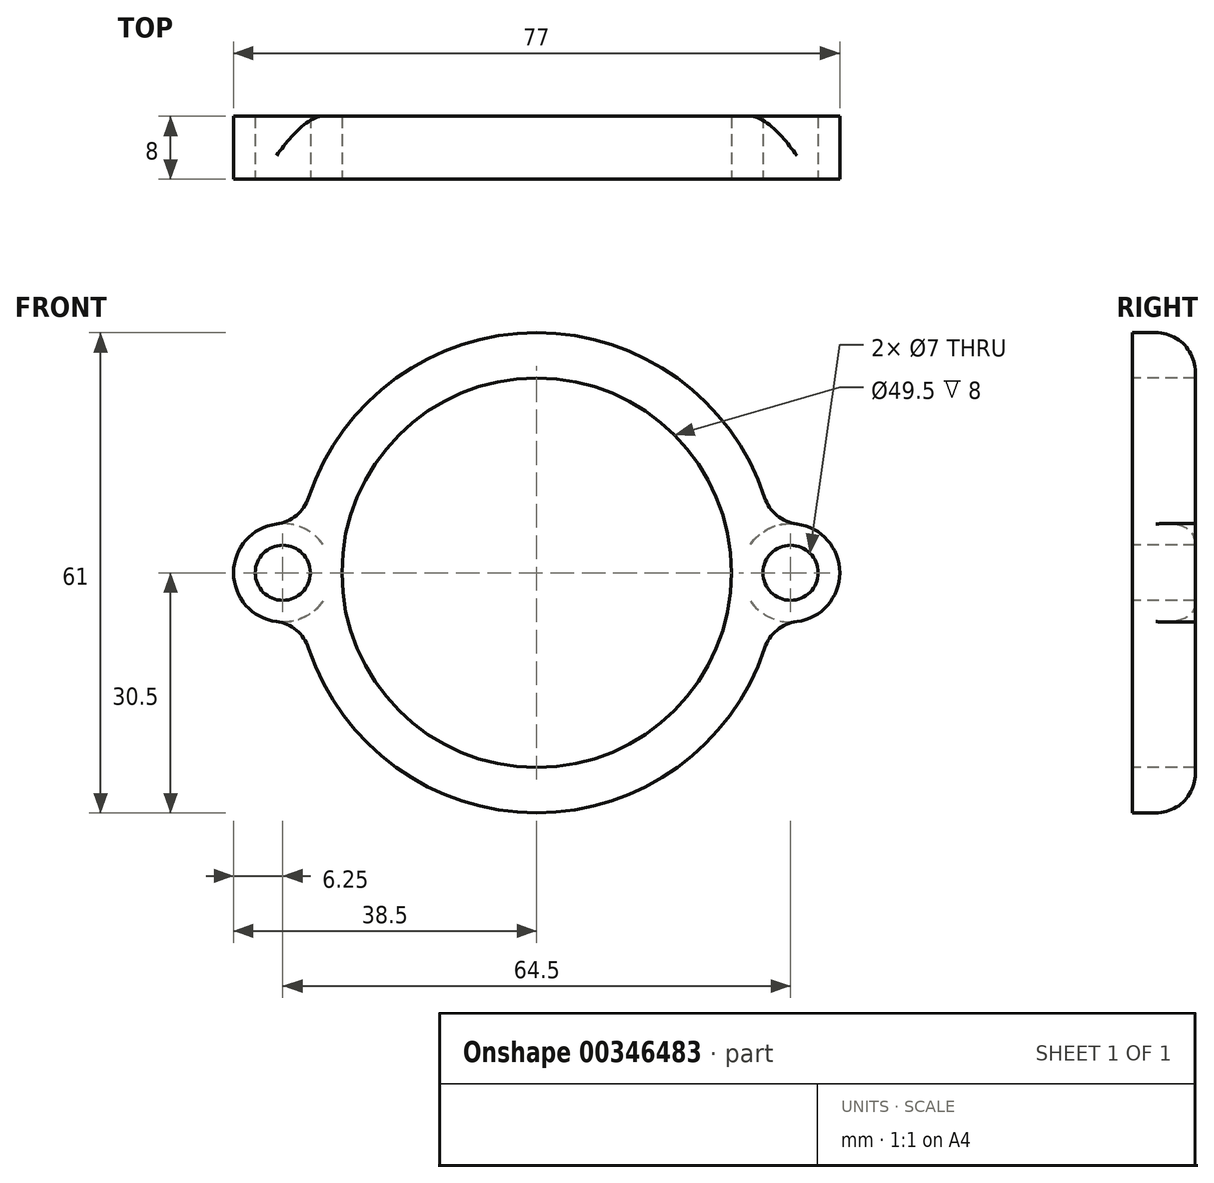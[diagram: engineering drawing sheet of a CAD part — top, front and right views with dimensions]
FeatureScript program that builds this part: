
annotation { "Feature Type Name" : "Feature", "Feature Type Description" : "" }
export const myFeature = defineFeature(function(context is Context, id is Id, definition is map)
    precondition{}
    {
        {
            var Q0;
            Q0=qCreatedBy(makeId("Front.planeOp"),FACE);
            var sketch = newSketch(context, id + "F0", { "sketchPlane" : qUnion([Q0])});
            skPoint(sketch, "E0", {"position": v(24.75, 0) * mm});
            skCircle(sketch, "E1", {"center": v(0, 0) * mm, "radius": 24.75 * mm});
            skArc(sketch, "E2", {"start": v(28.95, 9.58) * mm, "mid": v(0, 30.5) * mm, "end": v(-28.95, 9.58) * mm});
            skLineSegment(sketch, "E3", {"start": v(0, 0) * mm, "end": v(34.56, 0) * mm, "construction": true});
            skLineSegment(sketch, "E4", {"start": v(0, 0) * mm, "end": v(0, 40.66) * mm, "construction": true});
            skPoint(sketch, "E5", {"position": v(32.25, 0) * mm});
            skCircle(sketch, "E6", {"center": v(32.25, 0) * mm, "radius": 3.5 * mm});
            skArc(sketch, "E7", {"start": v(33.06, -6.2) * mm, "mid": v(38.5, 0) * mm, "end": v(33.06, 6.2) * mm});
            skPoint(sketch, "E8.visualSharp", {"position": v(29.94, 5.8) * mm});
            skArc(sketch, "E8.filletArc", {"start": v(28.95, 9.58) * mm, "mid": v(30.52, 7.3) * mm, "end": v(33.06, 6.2) * mm});
            skPoint(sketch, "E9.visualSharp", {"position": v(29.94, -5.8) * mm});
            skArc(sketch, "E9.filletArc", {"start": v(33.06, -6.2) * mm, "mid": v(30.52, -7.3) * mm, "end": v(28.95, -9.58) * mm});
            skArc(sketch, "E10.MirrorCS", {"start": v(-28.95, 9.58) * mm, "mid": v(-30.52, 7.3) * mm, "end": v(-33.06, 6.2) * mm});
            skCircle(sketch, "E11.MirrorC", {"center": v(-32.25, 0) * mm, "radius": 3.5 * mm});
            skArc(sketch, "E12.MirrorCS", {"start": v(-33.06, -6.2) * mm, "mid": v(-38.5, 0) * mm, "end": v(-33.06, 6.2) * mm});
            skArc(sketch, "E13.MirrorCS", {"start": v(-33.06, -6.2) * mm, "mid": v(-30.52, -7.3) * mm, "end": v(-28.95, -9.58) * mm});
            skArc(sketch, "E14.trimOffspring", {"start": v(-28.95, -9.58) * mm, "mid": v(0, -30.5) * mm, "end": v(28.95, -9.58) * mm});
            skCircle(sketch, "E15", {"center": v(32.25, 0) * mm, "radius": 6.25 * mm});
            skCircle(sketch, "E16", {"center": v(-32.25, 0) * mm, "radius": 6.25 * mm});
            skSolve(sketch);
        }
        {
            var Q0;
            Q0=makeQuery(id+"F0.imprint","IMPRINT",FACE,{"disambiguationData":[TD([[makeQuery(id+"F0.imprint","IMPRINT",EDGE,{"derivedFrom":sQuery(id+"F0.wireOp",EDGE,"E1")}),-1.0]])]});
            extrude(context, id + "F1", {"entities" : qUnion([Q0]), "oppositeDirection" : true, "depth" : 8 * mm});
        }
        {
            var Q0;
            Q0=qCreatedBy(makeId("Front.planeOp"),FACE);
            var sketch = newSketch(context, id + "F2", { "sketchPlane" : qUnion([Q0])});
            skCircle(sketch, "E17", {"center": v(32.25, 0) * mm, "radius": 3.5 * mm});
            skCircle(sketch, "E18", {"center": v(32.25, 0) * mm, "radius": 6.25 * mm});
            skCircle(sketch, "E19.MirrorC", {"center": v(-32.25, 0) * mm, "radius": 6.25 * mm});
            skCircle(sketch, "E20.MirrorC", {"center": v(-32.25, 0) * mm, "radius": 3.5 * mm});
            skSolve(sketch);
        }
        {
            var Q0;
            Q0=makeQuery(id+"F1.opExtrude","CAP_EDGE",EDGE,{"disambiguationData":[OSD([sQuery(id+"F0.wireOp",EDGE,"E9.filletArc")])],"isStart":false});
            var Q1;
            Q1=makeQuery(id+"F1.opExtrude","CAP_EDGE",EDGE,{"disambiguationData":[OSD([sQuery(id+"F0.wireOp",EDGE,"E14.trimOffspring")])],"isStart":false});
            var Q2;
            Q2=makeQuery(id+"F1.opExtrude","CAP_EDGE",EDGE,{"disambiguationData":[OSD([sQuery(id+"F0.wireOp",EDGE,"E2")])],"isStart":false});
            fillet(context, id + "F3", {"entities" : qUnion([Q0, Q1, Q2]), "radius" : 5 * mm, "tangentPropagation" : true, "allowEdgeOverflow" : false});
        }
        {
            var Q0;
            Q0 = qSketchRegion(id + "F2", true);
            extrude(context, id + "F4", {"entities" : qUnion([Q0]), "operationType" : NewBodyOperationType.ADD, "oppositeDirection" : true, "depth" : 8 * mm});
        }
    });
